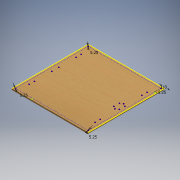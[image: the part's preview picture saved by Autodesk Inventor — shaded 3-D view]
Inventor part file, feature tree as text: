
AUTODESK INVENTOR PART (.ipt)
format: ipt  version: 2019 (Build 230136000, 136)  size: 166,400 bytes
history: native  units: in
note: dims shown in document units (in); Inventor stores cm internally (conversion verified against a paired STEP export)
features: extrude x2, sketch x1
ambient origin geometry x8: Origin, YZ Plane, XZ Plane, XY Plane, X Axis, Y Axis, Z Axis, Center Point
bodies: Solid1 (feature_tree)
feature tree (3):
  extrude  "Extrusion1"  Depth=0.3937in
  extrude  "Extrusion2"  Depth=0.3937in
  sketch  "Sketch1"  dims[d0=17.3228in d1=12.5984in d2=12.5984in d3=17.3228in d4=0.315in d5=0.0in d10=0.1969in d11=0.0in d28=0.2067in d29=0.2067in d30=0.2067in d31=0.2067in d32=0.3937in]
